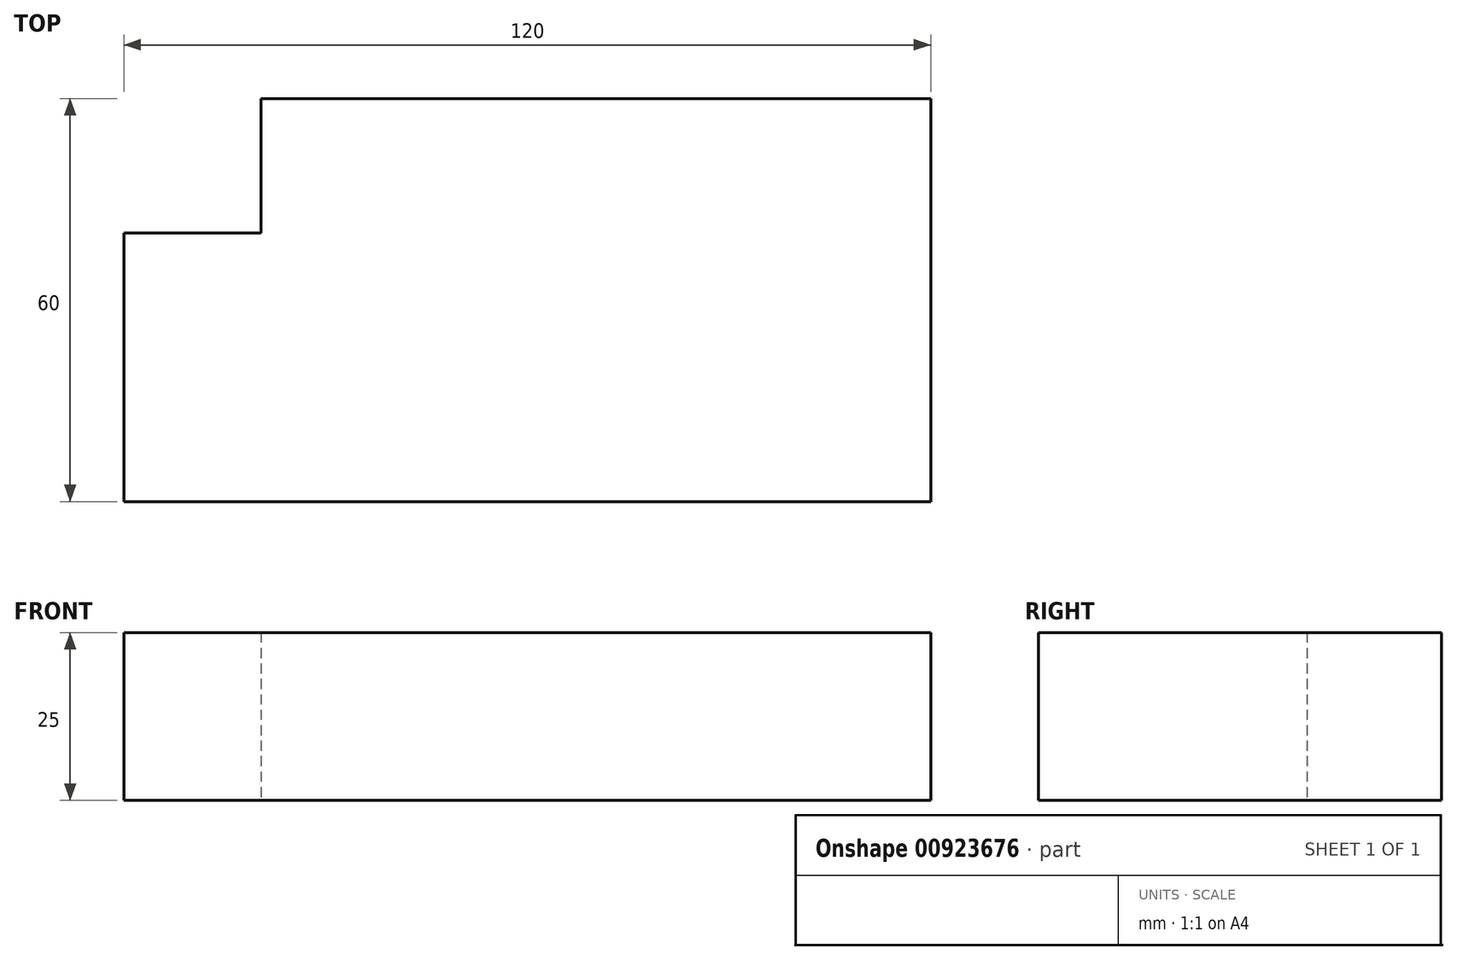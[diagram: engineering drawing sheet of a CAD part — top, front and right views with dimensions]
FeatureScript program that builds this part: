
annotation { "Feature Type Name" : "Feature", "Feature Type Description" : "" }
export const myFeature = defineFeature(function(context is Context, id is Id, definition is map)
    precondition{}
    {
        {
            var Q0;
            Q0=qCreatedBy(makeId("Top.planeOp"),FACE);
            var sketch = newSketch(context, id + "F0", { "sketchPlane" : qUnion([Q0])});
            skLineSegment(sketch, "E0.bottom", {"start": v(-64.75, 30) * mm, "end": v(55.25, 30) * mm});
            skLineSegment(sketch, "E0.top", {"start": v(-64.75, -30) * mm, "end": v(55.25, -30) * mm});
            skLineSegment(sketch, "E0.left", {"start": v(-64.75, 30) * mm, "end": v(-64.75, -30) * mm});
            skLineSegment(sketch, "E0.right", {"start": v(55.25, 30) * mm, "end": v(55.25, -30) * mm});
            skPoint(sketch, "E0.middle", {"position": v(-4.75, 0) * mm});
            skLineSegment(sketch, "E1.bottom", {"start": v(-64.75, 30) * mm, "end": v(-44.37, 30) * mm});
            skLineSegment(sketch, "E1.top", {"start": v(-64.75, 10) * mm, "end": v(-44.37, 10) * mm});
            skLineSegment(sketch, "E1.left", {"start": v(-64.75, 30) * mm, "end": v(-64.75, 10) * mm});
            skLineSegment(sketch, "E1.right", {"start": v(-44.37, 30) * mm, "end": v(-44.37, 10) * mm});
            skSolve(sketch);
        }
        {
            var Q0;
            {var subQ1=sQuery(id+"F0.wireOp",EDGE,"E0.top");Q0=makeQuery(id+"F0.imprint","IMPRINT",FACE,{"disambiguationData":[TD([[makeQuery(id+"F0.imprint","IMPRINT",EDGE,{"derivedFrom":subQ1}),1.0]])]});}
            extrude(context, id + "F1", {"entities" : qUnion([Q0]), "depth" : 25 * mm, "offsetDistance" : 25 * mm});
        }
    });
